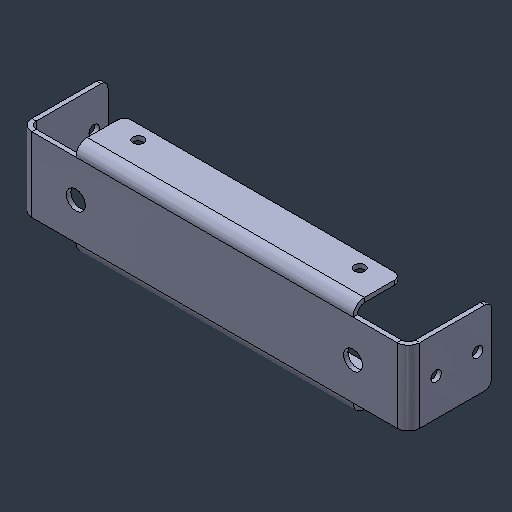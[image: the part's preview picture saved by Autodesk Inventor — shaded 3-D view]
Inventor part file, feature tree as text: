
AUTODESK INVENTOR PART (.ipt)
format: ipt  version: 2024.3 (Build 283343000, 343)  size: 133,120 bytes
history: native  units: mm (DEFAULTED — no unit token found)
features: fillet x1
ambient origin geometry x8: Origin, YZ Plane, XZ Plane, XY Plane, X Axis, Y Axis, Z Axis, Center Point
bodies: Solid1 (feature_tree)
feature tree (1):
  fillet  "Fillet1"  [1 undecoded]
note: 1 required parameter value undecoded (feature->parameter linkage not recoverable at this tier; creation-order binding heuristic only, values carry confidence <= 0.55)
